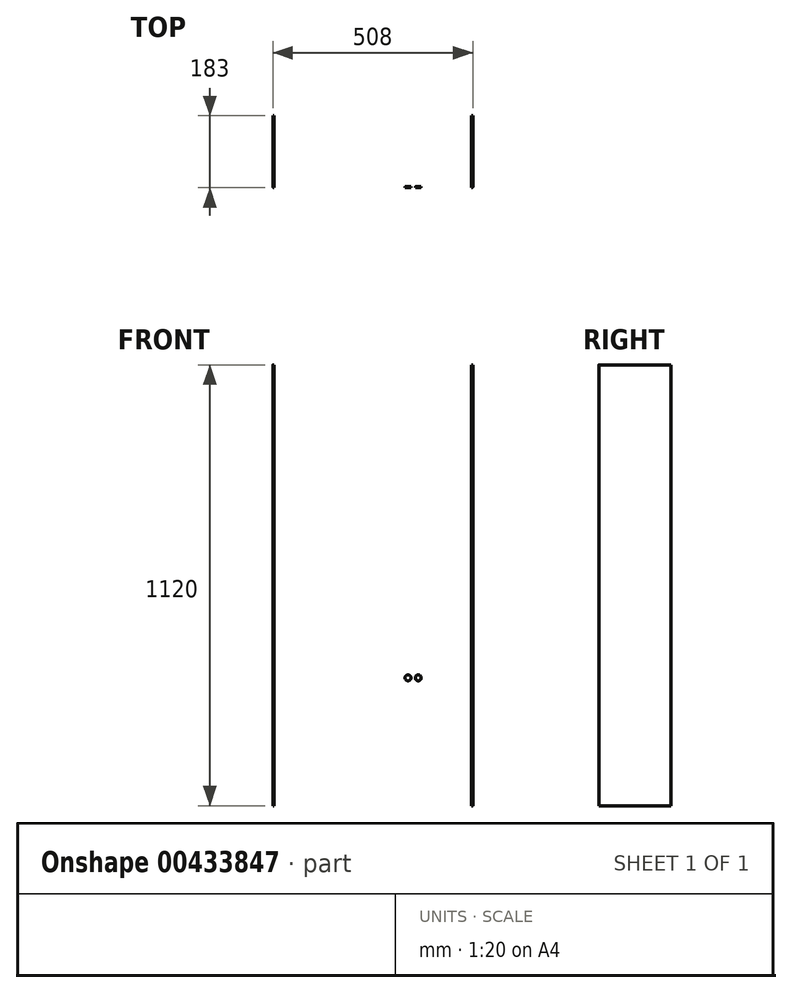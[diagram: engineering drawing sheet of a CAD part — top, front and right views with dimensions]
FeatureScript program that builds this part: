
annotation { "Feature Type Name" : "Feature", "Feature Type Description" : "" }
export const myFeature = defineFeature(function(context is Context, id is Id, definition is map)
    precondition{}
    {
        {
            var Q0;
            Q0=qCreatedBy(makeId("Top.planeOp"),FACE);
            var sketch = newSketch(context, id + "F0", { "sketchPlane" : qUnion([Q0])});
            skLineSegment(sketch, "E0", {"start": v(0, 0) * mm, "end": v(249, 0) * mm});
            skLineSegment(sketch, "E1", {"start": v(251, 2) * mm, "end": v(251, 180) * mm});
            skLineSegment(sketch, "E2", {"start": v(251, 180) * mm, "end": v(254, 180) * mm});
            skLineSegment(sketch, "E3", {"start": v(254, 180) * mm, "end": v(254, 0) * mm});
            skLineSegment(sketch, "E4", {"start": v(251, -3) * mm, "end": v(0, -3) * mm});
            skPoint(sketch, "E5.visualSharp", {"position": v(251, 0) * mm});
            skArc(sketch, "E5.filletArc", {"start": v(249, 0) * mm, "mid": v(250.41, 0.59) * mm, "end": v(251, 2) * mm});
            skPoint(sketch, "E6.visualSharp", {"position": v(254, -3) * mm});
            skArc(sketch, "E6.filletArc", {"start": v(251, -3) * mm, "mid": v(253.12, -2.12) * mm, "end": v(254, 0) * mm});
            skArc(sketch, "E7.MirrorCS", {"start": v(-249, 0) * mm, "mid": v(-250.41, 0.59) * mm, "end": v(-251, 2) * mm});
            skArc(sketch, "E8.MirrorCS", {"start": v(-251, -3) * mm, "mid": v(-253.12, -2.12) * mm, "end": v(-254, 0) * mm});
            skLineSegment(sketch, "E9.MirrorCS", {"start": v(-251, 180) * mm, "end": v(-254, 180) * mm});
            skLineSegment(sketch, "E10.MirrorCS", {"start": v(0, 0) * mm, "end": v(-249, 0) * mm});
            skLineSegment(sketch, "E11.MirrorCS", {"start": v(-251, 2) * mm, "end": v(-251, 180) * mm});
            skLineSegment(sketch, "E12.MirrorCS", {"start": v(-254, 180) * mm, "end": v(-254, 0) * mm});
            skLineSegment(sketch, "E13.MirrorCS", {"start": v(-251, -3) * mm, "end": v(0, -3) * mm});
            skPoint(sketch, "E14.MirrorP", {"position": v(-254, -3) * mm});
            skSolve(sketch);
        }
        {
            var Q0;
            Q0=makeQuery(id+"F0.imprint","IMPRINT",FACE,{"disambiguationData":[TD([[makeQuery(id+"F0.imprint","IMPRINT",EDGE,{"derivedFrom":sQuery(id+"F0.wireOp",EDGE,"E0")}),-1.0]])]});
            extrude(context, id + "F1", {"entities" : qUnion([Q0]), "depth" : 1120 * mm, "offsetDistance" : 25 * mm});
        }
        {
            var Q0;
            Q0=makeQuery(id+"F1.opExtrude","SWEPT_FACE",FACE,{"disambiguationData":[OSD([sQuery(id+"F0.wireOp",EDGE,"E4"),sQuery(id+"F0.wireOp",EDGE,"E13.MirrorCS")])]});
            var sketch = newSketch(context, id + "F2", { "sketchPlane" : qUnion([Q0])});
            skCircle(sketch, "E15", {"center": v(0, 225) * mm, "radius": 57.5 * mm});
            skSolve(sketch);
        }
        {
            var Q0;
            Q0=makeQuery(id+"F2.imprint","IMPRINT",FACE,{"disambiguationData":[TD([[makeQuery(id+"F2.imprint","IMPRINT",EDGE,{"derivedFrom":sQuery(id+"F2.wireOp",EDGE,"E15")}),1.0]])]});
            var Q1;
            Q1=sQuery(id+"F2.wireOp",EDGE,"E15");
            extrude(context, id + "F3", {"entities" : qUnion([Q0]), "operationType" : NewBodyOperationType.REMOVE, "surfaceEntities" : qUnion([Q1]), "endBound" : BoundingType.THROUGH_ALL, "oppositeDirection" : true, "depth" : 25 * mm});
        }
        {
            var Q0;
            Q0=makeQuery(id+"F1.opExtrude","SWEPT_FACE",FACE,{"disambiguationData":[OSD([sQuery(id+"F0.wireOp",EDGE,"E4"),sQuery(id+"F0.wireOp",EDGE,"E13.MirrorCS")])]});
            var sketch = newSketch(context, id + "F4", { "sketchPlane" : qUnion([Q0])});
            skCircle(sketch, "E16", {"center": v(0, 360.5) * mm, "radius": 32.5 * mm});
            skSolve(sketch);
        }
        {
            var Q0;
            Q0=makeQuery(id+"F4.imprint","IMPRINT",FACE,{"disambiguationData":[TD([[makeQuery(id+"F4.imprint","IMPRINT",EDGE,{"derivedFrom":sQuery(id+"F4.wireOp",EDGE,"E16")}),1.0]])]});
            var Q1;
            Q1=sQuery(id+"F4.wireOp",EDGE,"E16");
            extrude(context, id + "F5", {"entities" : qUnion([Q0]), "operationType" : NewBodyOperationType.REMOVE, "surfaceEntities" : qUnion([Q1]), "endBound" : BoundingType.THROUGH_ALL, "oppositeDirection" : true, "depth" : 25 * mm});
        }
        {
            var Q0;
            Q0=makeQuery(id+"F1.opExtrude","SWEPT_FACE",FACE,{"disambiguationData":[OSD([sQuery(id+"F0.wireOp",EDGE,"E4"),sQuery(id+"F0.wireOp",EDGE,"E13.MirrorCS")])]});
            var sketch = newSketch(context, id + "F6", { "sketchPlane" : qUnion([Q0])});
            skLineSegment(sketch, "E17", {"start": v(0, 927.5) * mm, "end": v(110, 927.5) * mm});
            skLineSegment(sketch, "E18", {"start": v(110, 927.5) * mm, "end": v(110, 1062.5) * mm});
            skLineSegment(sketch, "E19", {"start": v(110, 1062.5) * mm, "end": v(0, 1062.5) * mm});
            skLineSegment(sketch, "E20", {"start": v(0, 1062.5) * mm, "end": v(0, 927.5) * mm, "construction": true});
            skLineSegment(sketch, "E21.MirrorCS", {"start": v(-110, 1062.5) * mm, "end": v(0, 1062.5) * mm});
            skLineSegment(sketch, "E22.MirrorCS", {"start": v(-110, 927.5) * mm, "end": v(-110, 1062.5) * mm});
            skLineSegment(sketch, "E23.MirrorCS", {"start": v(0, 927.5) * mm, "end": v(-110, 927.5) * mm});
            skSolve(sketch);
        }
        {
            var Q0;
            Q0=makeQuery(id+"F6.imprint","IMPRINT",FACE,{"disambiguationData":[TD([[makeQuery(id+"F6.imprint","IMPRINT",EDGE,{"derivedFrom":sQuery(id+"F6.wireOp",EDGE,"E17")}),1.0]])]});
            extrude(context, id + "F7", {"entities" : qUnion([Q0]), "operationType" : NewBodyOperationType.REMOVE, "endBound" : BoundingType.THROUGH_ALL, "oppositeDirection" : true, "depth" : 25 * mm});
        }
        {
            var Q0;
            Q0=makeQuery(id+"F1.opExtrude","SWEPT_FACE",FACE,{"disambiguationData":[OSD([sQuery(id+"F0.wireOp",EDGE,"E4"),sQuery(id+"F0.wireOp",EDGE,"E13.MirrorCS")])]});
            var sketch = newSketch(context, id + "F8", { "sketchPlane" : qUnion([Q0])});
            skCircle(sketch, "E24", {"center": v(-89.5, 325) * mm, "radius": 7.5 * mm});
            skCircle(sketch, "E25", {"center": v(-115.5, 325) * mm, "radius": 7.5 * mm});
            skLineSegment(sketch, "E26", {"start": v(0, 282.5) * mm, "end": v(-172.44, 282.5) * mm, "construction": true});
            skLineSegment(sketch, "E27", {"start": v(0, 282.5) * mm, "end": v(0, 328) * mm, "construction": true});
            skCircle(sketch, "E28.MirrorC", {"center": v(89.5, 325) * mm, "radius": 7.5 * mm});
            skCircle(sketch, "E29.MirrorC", {"center": v(115.5, 325) * mm, "radius": 7.5 * mm});
            skSolve(sketch);
        }
        {
            var Q0;
            Q0=makeQuery(id+"F8.imprint","IMPRINT",FACE,{"disambiguationData":[TD([[makeQuery(id+"F8.imprint","IMPRINT",EDGE,{"derivedFrom":sQuery(id+"F8.wireOp",EDGE,"E25")}),1.0]])]});
            var Q1;
            Q1=makeQuery(id+"F8.imprint","IMPRINT",FACE,{"disambiguationData":[TD([[makeQuery(id+"F8.imprint","IMPRINT",EDGE,{"derivedFrom":sQuery(id+"F8.wireOp",EDGE,"E24")}),1.0]])]});
            var Q2;
            Q2=makeQuery(id+"F8.imprint","IMPRINT",FACE,{"disambiguationData":[TD([[makeQuery(id+"F8.imprint","IMPRINT",EDGE,{"derivedFrom":sQuery(id+"F8.wireOp",EDGE,"E28.MirrorC")}),-1.0]])]});
            var Q3;
            Q3=makeQuery(id+"F8.imprint","IMPRINT",FACE,{"disambiguationData":[TD([[makeQuery(id+"F8.imprint","IMPRINT",EDGE,{"derivedFrom":sQuery(id+"F8.wireOp",EDGE,"E29.MirrorC")}),-1.0]])]});
            var Q4;
            Q4=sQuery(id+"F8.wireOp",EDGE,"E25");
            var Q5;
            Q5=sQuery(id+"F8.wireOp",EDGE,"E24");
            extrude(context, id + "F9", {"entities" : qUnion([Q0, Q1, Q2, Q3]), "operationType" : NewBodyOperationType.REMOVE, "surfaceEntities" : qUnion([Q4, Q5]), "endBound" : BoundingType.THROUGH_ALL, "oppositeDirection" : true, "depth" : 25 * mm});
        }
    });
